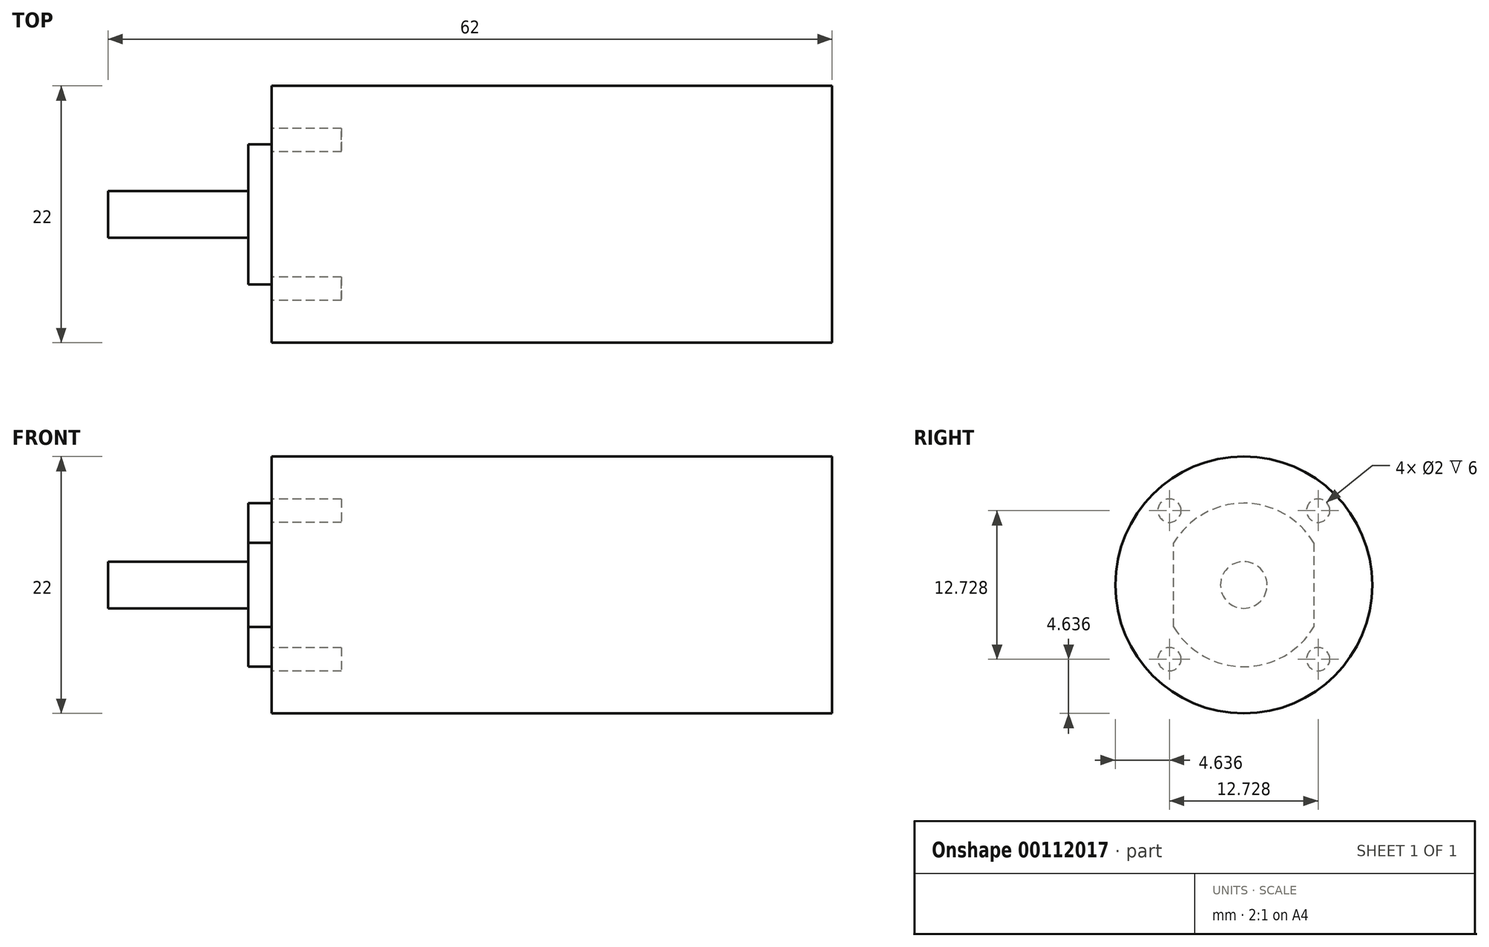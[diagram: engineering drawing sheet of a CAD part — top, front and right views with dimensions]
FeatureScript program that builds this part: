
annotation { "Feature Type Name" : "Feature", "Feature Type Description" : "" }
export const myFeature = defineFeature(function(context is Context, id is Id, definition is map)
    precondition{}
    {
        {
            var Q0;
            Q0=qCreatedBy(makeId("Right.planeOp"),FACE);
            var sketch = newSketch(context, id + "F0", { "sketchPlane" : qUnion([Q0])});
            skCircle(sketch, "E0", {"center": v(0, 0) * mm, "radius": 11 * mm});
            skSolve(sketch);
        }
        {
            var Q0;
            Q0=qSketchRegion(id+"F0",true);
            extrude(context, id + "F1", {"entities" : qUnion([Q0]), "depth" : 48 * mm});
        }
        {
            var Q0;
            Q0=makeQuery(id+"F1.opExtrude","CAP_FACE",FACE,{"disambiguationData":[OSD([sQuery(id+"F0.wireOp",EDGE,"E0")])],"isStart":true});
            var sketch = newSketch(context, id + "F2", { "sketchPlane" : qUnion([Q0])});
            skArc(sketch, "E1", {"start": v(-6, -3.6) * mm, "mid": v(0, -7) * mm, "end": v(6, -3.6) * mm});
            skLineSegment(sketch, "E2", {"start": v(-6, 3.6) * mm, "end": v(-6, -3.6) * mm});
            skLineSegment(sketch, "E3", {"start": v(6, -3.6) * mm, "end": v(6, 3.6) * mm});
            skArc(sketch, "E4.trimOffspring", {"start": v(6, 3.6) * mm, "mid": v(0, 7) * mm, "end": v(-6, 3.6) * mm});
            skSolve(sketch);
        }
        {
            var Q0;
            Q0=qSketchRegion(id+"F2",true);
            extrude(context, id + "F3", {"entities" : qUnion([Q0]), "operationType" : NewBodyOperationType.ADD, "depth" : 2 * mm});
        }
        {
            var Q0;
            Q0=makeQuery(id+"F3.opExtrude","CAP_FACE",FACE,{"disambiguationData":[OSD([sQuery(id+"F2.wireOp",EDGE,"E1"),sQuery(id+"F2.wireOp",EDGE,"E2"),sQuery(id+"F2.wireOp",EDGE,"E3"),sQuery(id+"F2.wireOp",EDGE,"E4.trimOffspring")])],"isStart":false});
            var sketch = newSketch(context, id + "F4", { "sketchPlane" : qUnion([Q0])});
            skCircle(sketch, "E5", {"center": v(0, 0) * mm, "radius": 2 * mm});
            skSolve(sketch);
        }
        {
            var Q0;
            Q0=qSketchRegion(id+"F4",true);
            extrude(context, id + "F5", {"entities" : qUnion([Q0]), "operationType" : NewBodyOperationType.ADD, "depth" : 12 * mm});
        }
        {
            var Q0;
            Q0=makeQuery(id+"F1.opExtrude","CAP_FACE",FACE,{"disambiguationData":[OSD([sQuery(id+"F0.wireOp",EDGE,"E0")])],"isStart":true});
            var sketch = newSketch(context, id + "F6", { "sketchPlane" : qUnion([Q0])});
            skCircle(sketch, "E6", {"center": v(6.36, 6.36) * mm, "radius": 1 * mm});
            skCircle(sketch, "E7", {"center": v(6.36, -6.36) * mm, "radius": 1 * mm});
            skCircle(sketch, "E8", {"center": v(-6.36, -6.36) * mm, "radius": 1 * mm});
            skCircle(sketch, "E9", {"center": v(-6.36, 6.36) * mm, "radius": 1 * mm});
            skLineSegment(sketch, "E10", {"start": v(-6.36, 6.36) * mm, "end": v(-6.36, -6.36) * mm, "construction": true});
            skLineSegment(sketch, "E11", {"start": v(-6.36, -6.36) * mm, "end": v(6.36, -6.36) * mm, "construction": true});
            skLineSegment(sketch, "E12", {"start": v(6.36, -6.36) * mm, "end": v(6.36, 6.36) * mm, "construction": true});
            skLineSegment(sketch, "E13", {"start": v(-6.36, 6.36) * mm, "end": v(0, 0) * mm, "construction": true});
            skLineSegment(sketch, "E14", {"start": v(6.36, -6.36) * mm, "end": v(0, 0) * mm, "construction": true});
            skSolve(sketch);
        }
        {
            var Q0;
            Q0=qSketchRegion(id+"F6",true);
            extrude(context, id + "F7", {"entities" : qUnion([Q0]), "operationType" : NewBodyOperationType.REMOVE, "oppositeDirection" : true, "depth" : 6 * mm});
        }
    });
